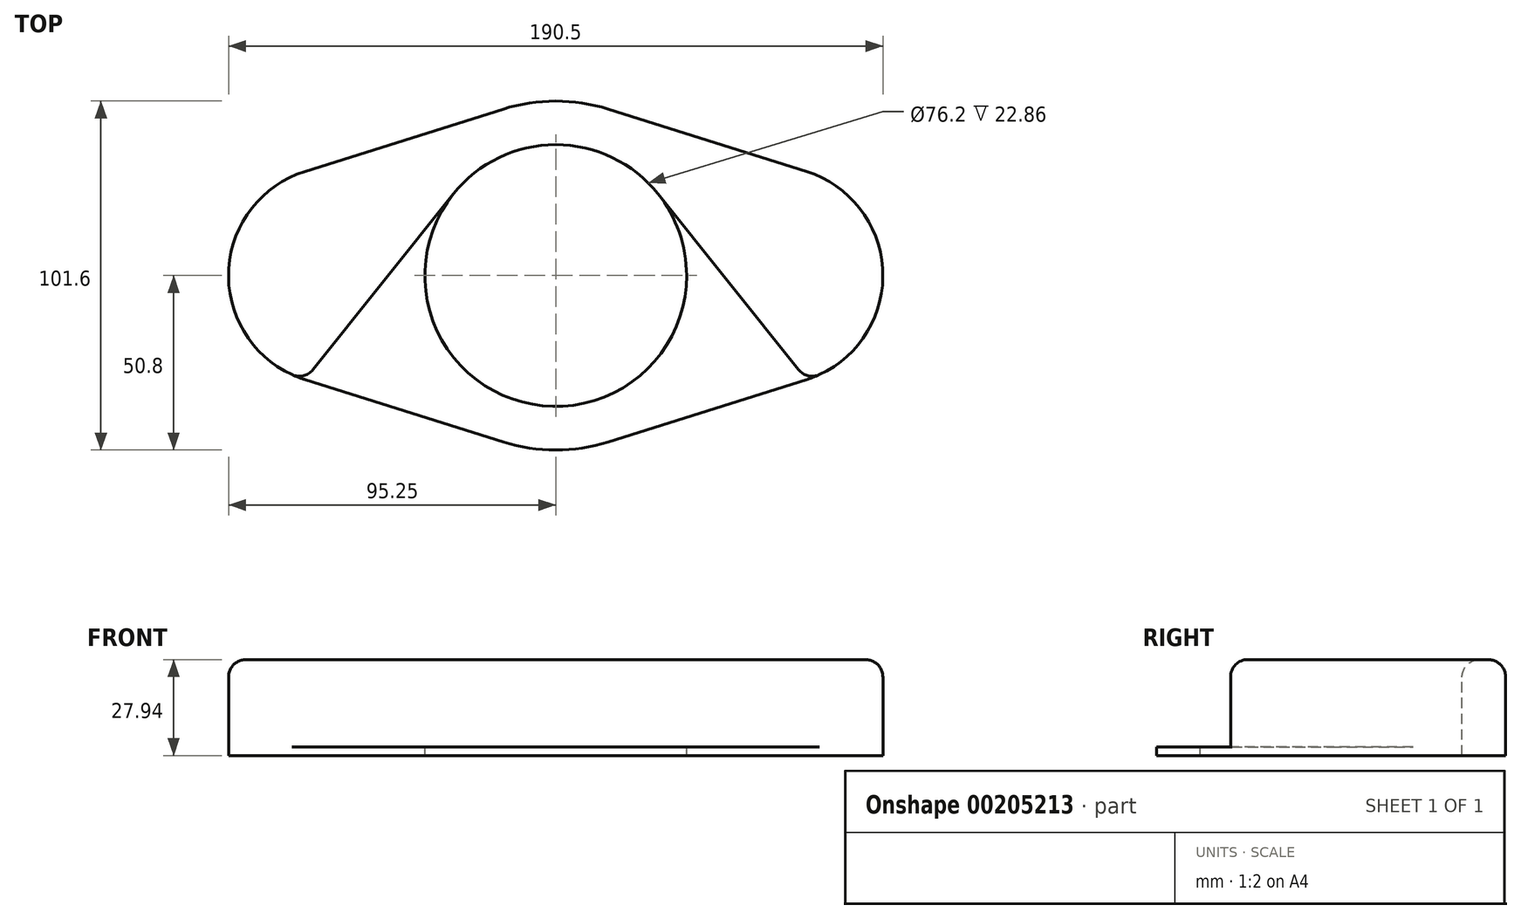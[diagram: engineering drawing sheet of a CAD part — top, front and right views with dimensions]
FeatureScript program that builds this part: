
annotation { "Feature Type Name" : "Feature", "Feature Type Description" : "" }
export const myFeature = defineFeature(function(context is Context, id is Id, definition is map)
    precondition{}
    {
        {
            var Q0;
            Q0=qCreatedBy(makeId("Top.planeOp"),FACE);
            var sketch = newSketch(context, id + "F4", { "sketchPlane" : qUnion([Q0])});
            skCircle(sketch, "E0", {"center": v(0, 0) * mm, "radius": 50.8 * mm});
            skLineSegment(sketch, "E1", {"start": v(-63.5, 0) * mm, "end": v(63.5, 0) * mm});
            skCircle(sketch, "E2", {"center": v(63.5, 0) * mm, "radius": 31.75 * mm});
            skCircle(sketch, "E3", {"center": v(-63.5, 0) * mm, "radius": 31.75 * mm});
            skLineSegment(sketch, "E4", {"start": v(-73.03, 30.29) * mm, "end": v(-15.24, 48.46) * mm});
            skLineSegment(sketch, "E5", {"start": v(-73.03, -30.29) * mm, "end": v(-15.24, -48.46) * mm});
            skLineSegment(sketch, "E6", {"start": v(73.03, -30.29) * mm, "end": v(15.24, -48.46) * mm});
            skLineSegment(sketch, "E7", {"start": v(73.03, 30.29) * mm, "end": v(15.24, 48.46) * mm});
            skSolve(sketch);
        }
        {
            var Q0;
            Q0 = qSketchRegion(id + "F4", true);
            var Q1;
            {var subQ0=sQuery(id+"F4.wireOp",EDGE,"E1");var subQ1=sQuery(id+"F4.wireOp",EDGE,"E0");var subQ2=makeQuery(id+"F4.imprint","INTERSECT",VERTEX,{"disambiguationData":[OD(0.0)],"derivedFrom":[subQ1,subQ0]});Q1=makeQuery(id+"F4.imprint","IMPRINT",FACE,{"disambiguationData":[TD([[makeQuery(id+"F4.imprint","IMPRINT",EDGE,{"disambiguationData":[TD([[subQ2,-1.0]])],"derivedFrom":subQ1}),1.0]])]});}
            var Q2;
            {var subQ0=sQuery(id+"F4.wireOp",EDGE,"E1");var subQ1=sQuery(id+"F4.wireOp",EDGE,"E0");var subQ2=makeQuery(id+"F4.imprint","INTERSECT",VERTEX,{"disambiguationData":[OD(0.0)],"derivedFrom":[subQ1,subQ0]});Q2=makeQuery(id+"F4.imprint","IMPRINT",FACE,{"disambiguationData":[TD([[makeQuery(id+"F4.imprint","IMPRINT",EDGE,{"disambiguationData":[TD([[subQ2,1.0]])],"derivedFrom":subQ1}),1.0]])]});}
            var Q3;
            {var subQ0=sQuery(id+"F4.wireOp",EDGE,"E1");var subQ1=sQuery(id+"F4.wireOp",EDGE,"E0");var subQ2=makeQuery(id+"F4.imprint","INTERSECT",VERTEX,{"disambiguationData":[OD(1.0)],"derivedFrom":[subQ1,subQ0]});Q3=makeQuery(id+"F4.imprint","IMPRINT",FACE,{"disambiguationData":[TD([[makeQuery(id+"F4.imprint","IMPRINT",EDGE,{"disambiguationData":[TD([[subQ2,-1.0]])],"derivedFrom":subQ1}),1.0]])]});}
            var Q4;
            {var subQ0=sQuery(id+"F4.wireOp",EDGE,"E1");var subQ1=sQuery(id+"F4.wireOp",EDGE,"E0");var subQ2=makeQuery(id+"F4.imprint","INTERSECT",VERTEX,{"disambiguationData":[OD(1.0)],"derivedFrom":[subQ1,subQ0]});Q4=makeQuery(id+"F4.imprint","IMPRINT",FACE,{"disambiguationData":[TD([[makeQuery(id+"F4.imprint","IMPRINT",EDGE,{"disambiguationData":[TD([[subQ2,1.0]])],"derivedFrom":subQ1}),1.0]])]});}
            extrude(context, id + "F0", {"entities" : qUnion([Q0, Q1, Q2, Q3, Q4]), "depth" : 2.54 * mm});
        }
        {
            var Q0;
            Q0=makeQuery(id+"F0.opExtrude","CAP_FACE",FACE,{"disambiguationData":[OSD([sQuery(id+"F4.wireOp",EDGE,"E0"),sQuery(id+"F4.wireOp",EDGE,"E2"),sQuery(id+"F4.wireOp",EDGE,"E3"),sQuery(id+"F4.wireOp",EDGE,"E4"),sQuery(id+"F4.wireOp",EDGE,"E5"),sQuery(id+"F4.wireOp",EDGE,"E6"),sQuery(id+"F4.wireOp",EDGE,"E7")])],"isStart":false});
            var sketch = newSketch(context, id + "F1", { "sketchPlane" : qUnion([Q0])});
            skCircle(sketch, "E8", {"center": v(0, 0) * mm, "radius": 38.1 * mm});
            skSolve(sketch);
        }
        {
            var Q0;
            Q0 = qSketchRegion(id + "F1", true);
            extrude(context, id + "F5", {"entities" : qUnion([Q0]), "operationType" : NewBodyOperationType.REMOVE, "endBound" : BoundingType.THROUGH_ALL, "oppositeDirection" : true, "depth" : 25.4 * mm});
        }
        {
            var Q0;
            Q0=makeQuery(id+"F0.opExtrude","CAP_FACE",FACE,{"disambiguationData":[OSD([sQuery(id+"F4.wireOp",EDGE,"E0"),sQuery(id+"F4.wireOp",EDGE,"E2"),sQuery(id+"F4.wireOp",EDGE,"E3"),sQuery(id+"F4.wireOp",EDGE,"E4"),sQuery(id+"F4.wireOp",EDGE,"E5"),sQuery(id+"F4.wireOp",EDGE,"E6"),sQuery(id+"F4.wireOp",EDGE,"E7")])],"isStart":false});
            var sketch = newSketch(context, id + "F6", { "sketchPlane" : qUnion([Q0])});
            skLineSegment(sketch, "E9", {"start": v(-29.75, 23.8) * mm, "end": v(-73.03, -30.29) * mm});
            skLineSegment(sketch, "E10", {"start": v(29.75, 23.8) * mm, "end": v(73.03, -30.29) * mm});
            skSolve(sketch);
        }
        {
            var Q0;
            {var subQ4=sQuery(id+"F6.wireOp",EDGE,"E9");Q0=makeQuery(id+"F6.imprint","IMPRINT",FACE,{"disambiguationData":[TD([[makeQuery(id+"F6.imprint","IMPRINT",EDGE,{"derivedFrom":subQ4}),-1.0]])]});}
            extrude(context, id + "F2", {"entities" : qUnion([Q0]), "operationType" : NewBodyOperationType.ADD, "depth" : 25.4 * mm});
        }
        {
            var Q0;
            Q0=makeQuery(id+"F2.opExtrude","SWEPT_EDGE",EDGE,{"disambiguationData":[OSD([sQuery(id+"F4.wireOp",EDGE,"E2"),sQuery(id+"F4.wireOp",EDGE,"E6"),sQuery(id+"F6.wireOp",EDGE,"E10")])]});
            var Q1;
            Q1=makeQuery(id+"F2.opExtrude","SWEPT_EDGE",EDGE,{"disambiguationData":[OSD([sQuery(id+"F4.wireOp",EDGE,"E3"),sQuery(id+"F4.wireOp",EDGE,"E5"),sQuery(id+"F6.wireOp",EDGE,"E9")])]});
            var Q2;
            Q2=makeQuery(id+"F2.opExtrude","CAP_FACE",FACE,{"disambiguationData":[OSD([sQuery(id+"F4.wireOp",EDGE,"E0"),sQuery(id+"F4.wireOp",EDGE,"E2"),sQuery(id+"F4.wireOp",EDGE,"E3"),sQuery(id+"F4.wireOp",EDGE,"E4"),sQuery(id+"F4.wireOp",EDGE,"E7"),sQuery(id+"F1.wireOp",EDGE,"E8"),sQuery(id+"F6.wireOp",EDGE,"E9"),sQuery(id+"F6.wireOp",EDGE,"E10")])],"isStart":false});
            fillet(context, id + "F3", {"entities" : qUnion([Q0, Q1, Q2]), "radius" : 5.08 * mm, "tangentPropagation" : true, "allowEdgeOverflow" : false});
        }
    });
